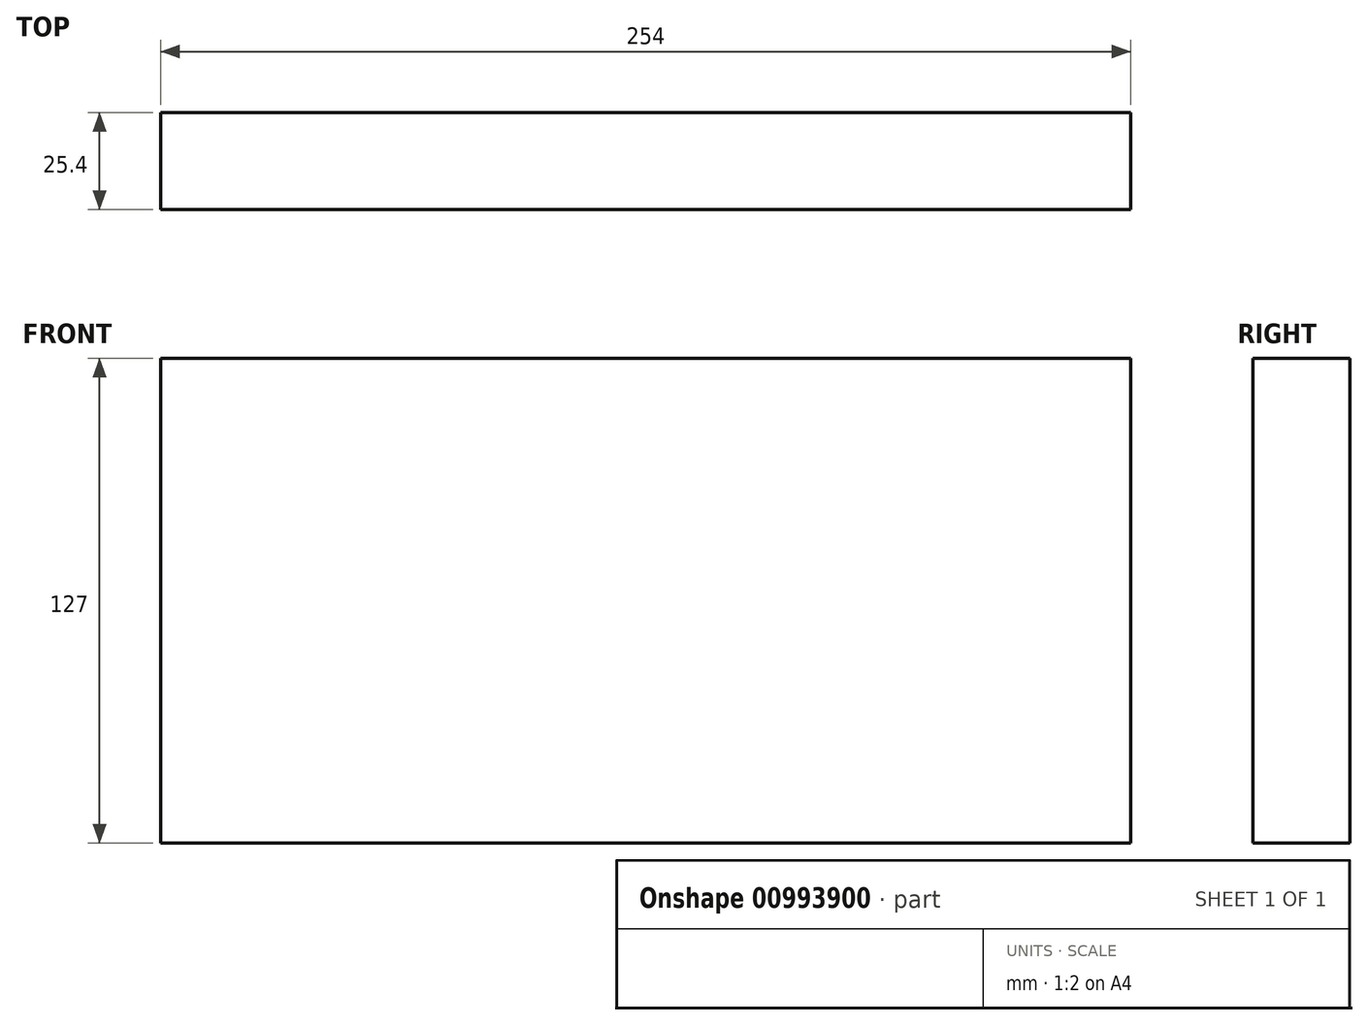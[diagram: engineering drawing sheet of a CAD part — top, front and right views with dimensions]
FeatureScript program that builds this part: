
annotation { "Feature Type Name" : "Feature", "Feature Type Description" : "" }
export const myFeature = defineFeature(function(context is Context, id is Id, definition is map)
    precondition{}
    {
        {
            var Q0;
            Q0=qCreatedBy(makeId("Front.planeOp"),FACE);
            var sketch = newSketch(context, id + "F0", { "sketchPlane" : qUnion([Q0])});
            skLineSegment(sketch, "E0.bottom", {"start": v(0, 0) * mm, "end": v(254, 0) * mm});
            skLineSegment(sketch, "E0.top", {"start": v(0, 127) * mm, "end": v(254, 127) * mm});
            skLineSegment(sketch, "E0.left", {"start": v(0, 0) * mm, "end": v(0, 127) * mm});
            skLineSegment(sketch, "E0.right", {"start": v(254, 0) * mm, "end": v(254, 127) * mm});
            skSolve(sketch);
        }
        {
            var Q0;
            Q0=makeQuery(id+"F0.imprint","IMPRINT",FACE,{"disambiguationData":[TD([[makeQuery(id+"F0.imprint","IMPRINT",EDGE,{"derivedFrom":sQuery(id+"F0.wireOp",EDGE,"E0.bottom")}),1.0]])]});
            extrude(context, id + "F1", {"entities" : qUnion([Q0]), "depth" : 25.4 * mm, "offsetDistance" : 25.4 * mm});
        }
    });
